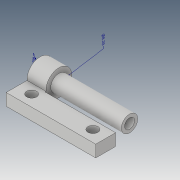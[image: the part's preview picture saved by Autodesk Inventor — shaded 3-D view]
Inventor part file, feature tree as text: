
AUTODESK INVENTOR PART (.ipt)
format: ipt  version: 2019 (Build 230136000, 136)  size: 185,856 bytes
history: native  units: mm
features: extrude x7, other x6, sketch x6, plane x5, move_body x2, fillet x1, direct_edit x1, projected_geometry x1
ambient origin geometry x8: Origin, YZ Plane, XZ Plane, XY Plane, X Axis, Y Axis, Z Axis, Center Point
bodies: Solid1 (feature_tree)
feature tree (29):
  other  "Annotations"
  extrude  "Extrusion1"  Depth=45.0mm
  sketch  "Sketch4"  dims[d5=5.0mm d6=5.0mm d7=11.0mm]
  extrude  "Extrusion4"  Depth=5.0mm
  fillet  "Fillet1"  Radius=11.0mm
  extrude  "Extrusion5"  Depth=23.0mm
  plane  "Work Plane1"
  extrude  "Extrusion6"  Depth=10.0mm
  plane  "Work Plane8"
  plane  "Work Plane10"
  sketch  "Sketch11"  dims[d24=3.0mm d25=0.0mm d26=12.0mm]
  plane  "Work Plane11"
  plane  "Work Plane12"
  extrude  "Extrusion10"  Depth=12.0mm
  extrude  "Extrusion11"  Depth=6.5mm TaperAngle=0.0deg
  direct_edit  "Direct Edit1"
  extrude  "Extrusion13"  Depth=6.5mm
  sketch  "Sketch1"  dims[d0=6.0mm d1=0.0mm d4=45.0mm]
  sketch  "Sketch5"  dims[d8=11.0mm d9=23.0mm]
  sketch  "Sketch6"  dims[d10=10.0mm d20=13.0mm]
  projected_geometry  "Projected Loop4"
  sketch  "Sketch13"  dims[d27=5.0mm d28=3.0mm d29=0.0mm d33=5.0mm d34=5.0mm d35=17.8mm d36=7.0mm d37=17.8mm d38=7.1mm d39=30.8mm d40=7.1mm d41=3.0mm d42=0.0mm d52=0.0mm d53=0.0mm d54=0.0mm d55=10.0mm d56=0.0mm d57=10.0mm d58=0.0mm d59=0.0mm d60=0.0mm d61=-1.5mm d62=0.0mm d63=0.0mm d64=-17.25mm d68=1.6mm d69=10.0mm d70=0.0mm d71=35.626875mm d72=6.5mm d75=48.705644mm d76=8.2mm]
  move_body  "Move1"
  move_body  "Move2"
  other  "Radial Dimension 1"
  other  "Diameter Dimension 1"
  parser-record x1  (decoder bookkeeping rows leaked as tree rows — omitted from the tree; the rows remain in map.json)
  other  "Cerniera Assemb.iam"
  other  "Cerniera 1:2"
note: 1 file-system path scrubbed to <path> (originals preserved in map.json)
